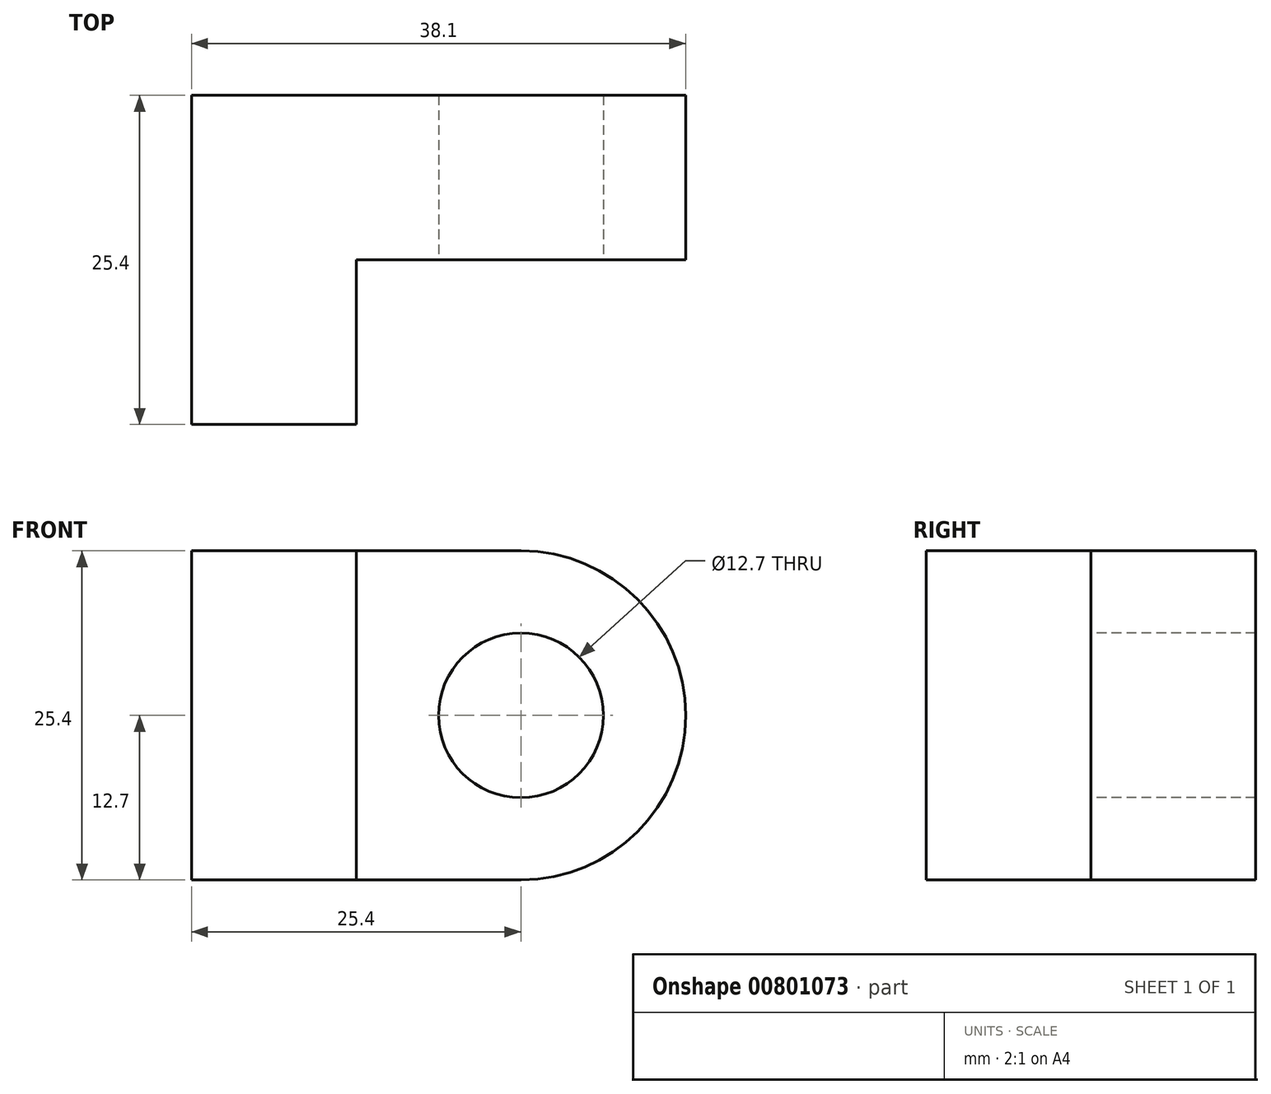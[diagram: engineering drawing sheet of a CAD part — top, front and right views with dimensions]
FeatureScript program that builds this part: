
annotation { "Feature Type Name" : "Feature", "Feature Type Description" : "" }
export const myFeature = defineFeature(function(context is Context, id is Id, definition is map)
    precondition{}
    {
        {
            var Q0;
            Q0=qCreatedBy(makeId("Front.planeOp"),FACE);
            var sketch = newSketch(context, id + "F0", { "sketchPlane" : qUnion([Q0])});
            skLineSegment(sketch, "E0", {"start": v(0, 0) * mm, "end": v(38.1, 0) * mm});
            skLineSegment(sketch, "E1", {"start": v(38.1, 0) * mm, "end": v(38.1, 25.4) * mm});
            skLineSegment(sketch, "E2", {"start": v(38.1, 25.4) * mm, "end": v(0, 25.4) * mm});
            skLineSegment(sketch, "E3", {"start": v(0, 25.4) * mm, "end": v(0, 0) * mm});
            skSolve(sketch);
        }
        {
            var Q0;
            Q0 = qSketchRegion(id + "F0", true);
            extrude(context, id + "F1", {"entities" : qUnion([Q0]), "depth" : 25.4 * mm, "offsetDistance" : 25.4 * mm});
        }
        {
            var Q0;
            Q0=makeQuery(id+"F1.opExtrude","CAP_FACE",FACE,{"disambiguationData":[OSD([sQuery(id+"F0.wireOp",EDGE,"E0"),sQuery(id+"F0.wireOp",EDGE,"E1"),sQuery(id+"F0.wireOp",EDGE,"E2"),sQuery(id+"F0.wireOp",EDGE,"E3")])],"isStart":false});
            var sketch = newSketch(context, id + "F2", { "sketchPlane" : qUnion([Q0])});
            skLineSegment(sketch, "E4", {"start": v(0, 25.4) * mm, "end": v(12.7, 25.4) * mm, "construction": true});
            skLineSegment(sketch, "E5", {"start": v(12.7, 25.4) * mm, "end": v(12.7, 0) * mm});
            skSolve(sketch);
        }
        {
            var Q0;
            Q0 = qSketchRegion(id + "F2", true);
            var Q1;
            {var subQ0=sQuery(id+"F2.wireOp",EDGE,"E5");Q1=makeQuery(id+"F2.imprint","IMPRINT",FACE,{"disambiguationData":[TD([[makeQuery(id+"F2.imprint","IMPRINT",EDGE,{"derivedFrom":subQ0}),1.0]])]});}
            extrude(context, id + "F3", {"entities" : qUnion([Q0, Q1]), "operationType" : NewBodyOperationType.REMOVE, "oppositeDirection" : true, "depth" : 12.7 * mm, "offsetDistance" : 25.4 * mm});
        }
        {
            var Q0;
            Q0=makeQuery(id+"F3.boolean.opBoolean","COPY",FACE,{"derivedFrom":makeQuery(id+"F3.opExtrude","CAP_FACE",FACE,{"disambiguationData":[OSD([sQuery(id+"F0.wireOp",EDGE,"E0"),sQuery(id+"F0.wireOp",EDGE,"E1"),sQuery(id+"F0.wireOp",EDGE,"E2"),sQuery(id+"F2.wireOp",EDGE,"E5")])],"isStart":false})});
            var sketch = newSketch(context, id + "F4", { "sketchPlane" : qUnion([Q0])});
            skArc(sketch, "E6", {"start": v(25.4, 0) * mm, "mid": v(38.1, 12.7) * mm, "end": v(25.4, 25.4) * mm});
            skCircle(sketch, "E7", {"center": v(25.4, 12.7) * mm, "radius": 6.35 * mm});
            skSolve(sketch);
        }
        {
            var Q0;
            Q0 = qSketchRegion(id + "F4", true);
            var Q1;
            {var subQ0=sQuery(id+"F4.wireOp",EDGE,"E6");var subQ1=makeQuery(id+"F3.boolean.opBoolean","COPY",EDGE,{"derivedFrom":makeQuery(id+"F3.opExtrude","CAP_EDGE",EDGE,{"disambiguationData":[OSD([sQuery(id+"F0.wireOp",EDGE,"E2")])],"isStart":false})});var subQ2=makeQuery(id+"F4.imprint","INTERSECT",VERTEX,{"derivedFrom":[subQ1,subQ0]});Q1=makeQuery(id+"F4.imprint","IMPRINT",FACE,{"disambiguationData":[TD([[makeQuery(id+"F4.imprint","IMPRINT",EDGE,{"disambiguationData":[TD([[subQ2,1.0]])],"derivedFrom":subQ0}),-1.0]])]});}
            var Q2;
            {var subQ0=sQuery(id+"F4.wireOp",EDGE,"E6");var subQ1=makeQuery(id+"F3.boolean.opBoolean","COPY",EDGE,{"derivedFrom":makeQuery(id+"F3.opExtrude","CAP_EDGE",EDGE,{"disambiguationData":[OSD([sQuery(id+"F0.wireOp",EDGE,"E0")])],"isStart":false})});var subQ2=makeQuery(id+"F4.imprint","INTERSECT",VERTEX,{"derivedFrom":[subQ1,subQ0]});Q2=makeQuery(id+"F4.imprint","IMPRINT",FACE,{"disambiguationData":[TD([[makeQuery(id+"F4.imprint","IMPRINT",EDGE,{"disambiguationData":[TD([[subQ2,-1.0]])],"derivedFrom":subQ0}),-1.0]])]});}
            extrude(context, id + "F5", {"entities" : qUnion([Q0, Q1, Q2]), "operationType" : NewBodyOperationType.REMOVE, "endBound" : BoundingType.UP_TO_NEXT, "oppositeDirection" : true, "depth" : 25.4 * mm, "offsetDistance" : 25.4 * mm});
        }
    });
